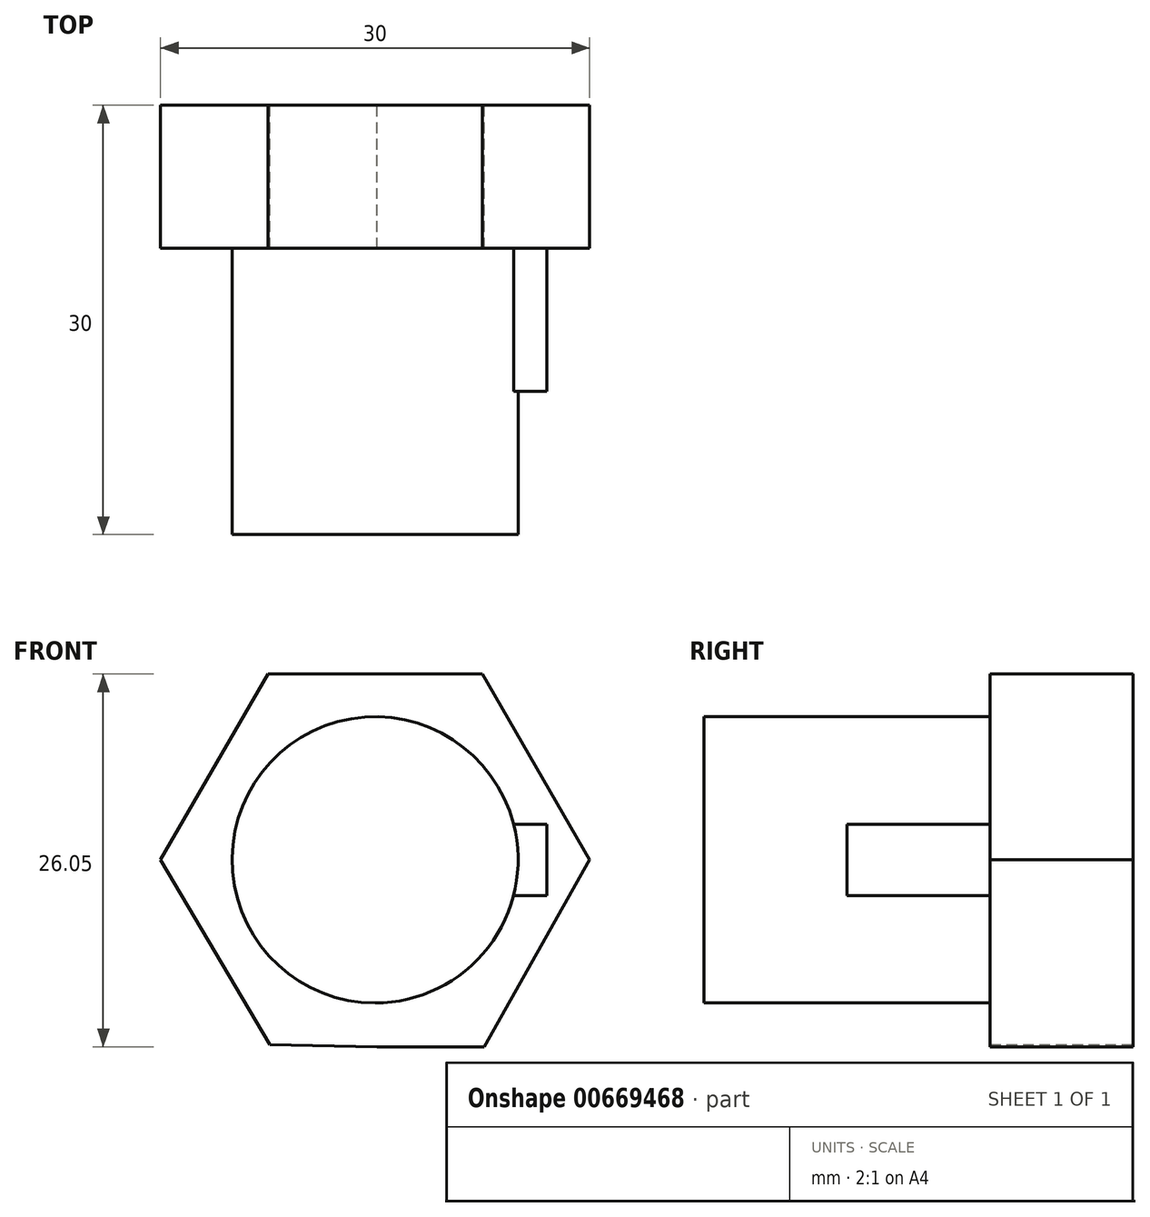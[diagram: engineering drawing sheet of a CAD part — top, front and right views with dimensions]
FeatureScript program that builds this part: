
annotation { "Feature Type Name" : "Feature", "Feature Type Description" : "" }
export const myFeature = defineFeature(function(context is Context, id is Id, definition is map)
    precondition{}
    {
        {
            var Q0;
            Q0=qCreatedBy(makeId("Front.planeOp"),FACE);
            var sketch = newSketch(context, id + "F0", { "sketchPlane" : qUnion([Q0])});
            skCircle(sketch, "E0", {"center": v(0, 0) * mm, "radius": 10 * mm});
            skLineSegment(sketch, "E1", {"start": v(0, 13) * mm, "end": v(7.5, 13) * mm});
            skLineSegment(sketch, "E2", {"start": v(0, 13) * mm, "end": v(-7.5, 13) * mm});
            skLineSegment(sketch, "E3", {"start": v(0.13, -13.06) * mm, "end": v(-7.37, -12.91) * mm});
            skLineSegment(sketch, "E4", {"start": v(0.13, -13.06) * mm, "end": v(7.63, -13.06) * mm});
            skLineSegment(sketch, "E5", {"start": v(15, 0) * mm, "end": v(7.63, -13.06) * mm});
            skLineSegment(sketch, "E6", {"start": v(15, 0) * mm, "end": v(7.5, 13) * mm});
            skLineSegment(sketch, "E7", {"start": v(-15, 0) * mm, "end": v(-7.5, 13) * mm});
            skLineSegment(sketch, "E8", {"start": v(-15, 0) * mm, "end": v(-7.37, -12.91) * mm});
            skLineSegment(sketch, "E9", {"start": v(12, 0) * mm, "end": v(12, 2.5) * mm});
            skLineSegment(sketch, "E10", {"start": v(12, 0) * mm, "end": v(12, -2.5) * mm});
            skLineSegment(sketch, "E11", {"start": v(12, -2.5) * mm, "end": v(9.68, -2.5) * mm});
            skLineSegment(sketch, "E12", {"start": v(12, 2.5) * mm, "end": v(9.68, 2.5) * mm});
            skSolve(sketch);
        }
        {
            var Q0;
            {var subQ0=sQuery(id+"F0.wireOp",EDGE,"E0");var subQ1=makeQuery(id+"F0.imprint","INTERSECT",VERTEX,{"derivedFrom":[subQ0,sQuery(id+"F0.wireOp",EDGE,"E11")]});Q0=makeQuery(id+"F0.imprint","IMPRINT",FACE,{"disambiguationData":[TD([[makeQuery(id+"F0.imprint","IMPRINT",EDGE,{"disambiguationData":[TD([[subQ1,1.0]])],"derivedFrom":subQ0}),1.0]])]});}
            extrude(context, id + "F1", {"entities" : qUnion([Q0]), "depth" : 30 * mm, "offsetDistance" : 25 * mm});
        }
        {
            var Q0;
            Q0=makeQuery(id+"F0.imprint","IMPRINT",FACE,{"disambiguationData":[TD([[makeQuery(id+"F0.imprint","IMPRINT",EDGE,{"derivedFrom":sQuery(id+"F0.wireOp",EDGE,"E1")}),-1.0]])]});
            extrude(context, id + "F2", {"entities" : qUnion([Q0]), "operationType" : NewBodyOperationType.ADD, "depth" : 10 * mm, "offsetDistance" : 25 * mm});
        }
        {
            var Q0;
            Q0=makeQuery(id+"F0.imprint","IMPRINT",FACE,{"disambiguationData":[TD([[makeQuery(id+"F0.imprint","IMPRINT",EDGE,{"derivedFrom":sQuery(id+"F0.wireOp",EDGE,"E9")}),1.0]])]});
            extrude(context, id + "F3", {"entities" : qUnion([Q0]), "operationType" : NewBodyOperationType.ADD, "depth" : 20 * mm, "offsetDistance" : 25 * mm});
        }
    });
